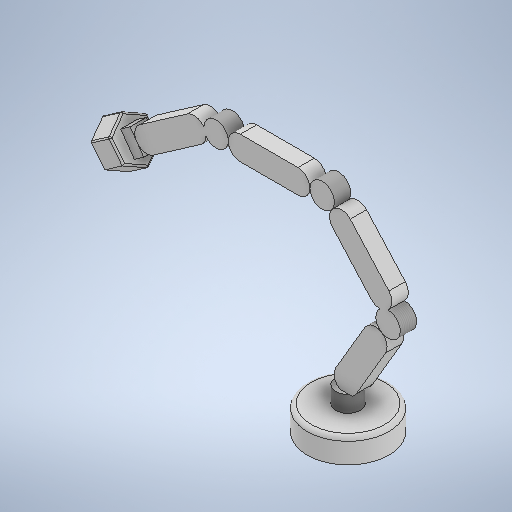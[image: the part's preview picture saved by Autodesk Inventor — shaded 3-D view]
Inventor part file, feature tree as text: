
AUTODESK INVENTOR PART (.ipt)
format: ipt  version: 2025.2 (Build 292293000, 293)  size: 524,800 bytes
history: native  units: mm
features: sketch x14, extrude x12, thread x6, fillet x5, projected_geometry x2
ambient origin geometry x8: Origin, YZ Plane, XZ Plane, XY Plane, X Axis, Y Axis, Z Axis, Center Point
bodies: Solid1 (feature_tree)
feature tree (39):
  extrude  "Extrusion1"  Depth=30.0mm TaperAngle=0.0deg
  extrude  "Extrusion2"  Depth=20.0mm TaperAngle=0.0deg
  extrude  "Extrusion3"  Depth=20.0mm TaperAngle=0.0deg
  extrude  "Extrusion4"  Depth=20.0mm TaperAngle=0.0deg
  thread  "Thread1"  [1 undecoded]
  thread  "Thread2"  [1 undecoded]
  fillet  "Fillet1"  Radius=5.0mm
  extrude  "Extrusion5"  Depth=29.225mm
  extrude  "Extrusion6"  Depth=30.0mm
  thread  "Thread3"  [1 undecoded]
  extrude  "Extrusion7"  Depth=100.0mm
  extrude  "Extrusion8"  Depth=20.0mm TaperAngle=0.0deg
  thread  "Thread4"  [1 undecoded]
  extrude  "Extrusion9"  Depth=20.0mm TaperAngle=0.0deg
  sketch  "Sketch11"  dims[d35=100.0mm d36=29.225mm]
  sketch  "Sketch12"  dims[d37=20.0mm d38=0.0mm d39=29.225mm d40=0.0mm]
  extrude  "Extrusion10"  Depth=29.225mm
  extrude  "Extrusion11"  Depth=29.225mm TaperAngle=0.0deg
  extrude  "Extrusion12"  Depth=2.0mm TaperAngle=0.0deg
  thread  "Thread5"  [1 undecoded]
  fillet  "Fillet2"  Radius=2.0mm
  thread  "Thread6"  [1 undecoded]
  fillet  "Fillet3"  Radius=2.0mm
  fillet  "Fillet4"  Radius=2.0mm
  fillet  "Fillet5"  Radius=2.0mm
  sketch  "Sketch1"  dims[d0=100.0mm d1=30.0mm d2=0.0mm]
  sketch  "Sketch2"  dims[d3=30.0mm d4=20.0mm d5=0.0mm]
  sketch  "Sketch3"  dims[d6=100.0mm d7=20.0mm d8=0.0mm]
  sketch  "Sketch4"  dims[d9=30.0mm d10=20.0mm d11=0.0mm d12=20.0mm d13=0.0mm d14=20.0mm d15=0.0mm d16=5.0mm]
  sketch  "Sketch5"  dims[d17=100.0mm d18=29.225mm]
  sketch  "Sketch6"  dims[d19=20.0mm d20=0.0mm d21=30.0mm d22=20.0mm d23=0.0mm]
  sketch  "Sketch7"  dims[d24=20.0mm d25=0.0mm d26=100.0mm]
  sketch  "Sketch8"  dims[d27=29.225mm d28=20.0mm d29=0.0mm d30=30.0mm]
  sketch  "Sketch9"  dims[d31=20.0mm d32=0.0mm d33=20.0mm d34=0.0mm]
  sketch  "Sketch13"  dims[d41=30.0mm d42=0.0mm d43=15.0mm d44=0.0mm d45=20.0mm d46=0.0mm d47=2.0mm d48=20.0mm d49=0.0mm d50=2.0mm d51=2.0mm d52=2.0mm]
  sketch  "Sketch14"
  projected_geometry  "Projected Loop1"
  sketch  "Sketch15"
  projected_geometry  "Projected Loop2"
note: 6 required parameter values undecoded (feature->parameter linkage not recoverable at this tier; creation-order binding heuristic only, values carry confidence <= 0.55)
